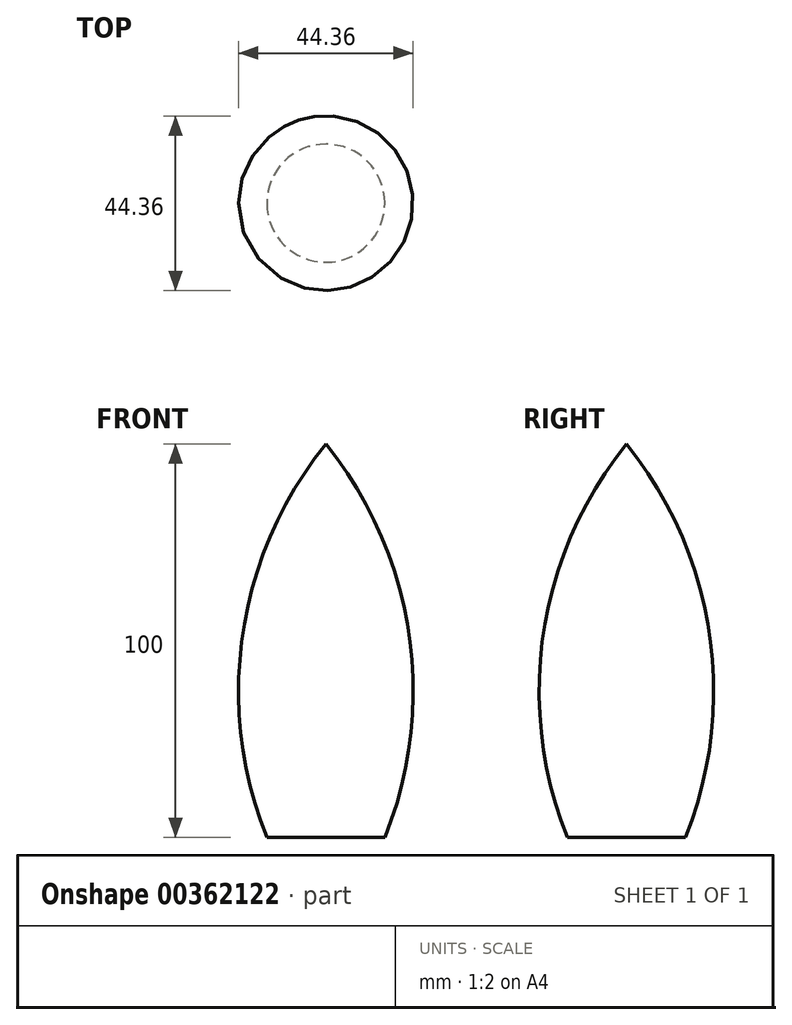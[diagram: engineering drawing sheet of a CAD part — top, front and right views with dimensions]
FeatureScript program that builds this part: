
annotation { "Feature Type Name" : "Feature", "Feature Type Description" : "" }
export const myFeature = defineFeature(function(context is Context, id is Id, definition is map)
    precondition{}
    {
        {
            var Q0;
            Q0=qCreatedBy(makeId("Front.planeOp"),FACE);
            var sketch = newSketch(context, id + "F0", { "sketchPlane" : qUnion([Q0])});
            skArc(sketch, "E0", {"start": v(0, 100) * mm, "mid": v(-21.07, 52.04) * mm, "end": v(-15, 0) * mm});
            skLineSegment(sketch, "E1", {"start": v(0, 100) * mm, "end": v(0, 0) * mm});
            skLineSegment(sketch, "E2", {"start": v(0, 0) * mm, "end": v(-15, 0) * mm});
            skSolve(sketch);
        }
        {
            var Q0;
            Q0=makeQuery(id+"F0.imprint","IMPRINT",FACE,{"disambiguationData":[TD([[makeQuery(id+"F0.imprint","IMPRINT",EDGE,{"derivedFrom":sQuery(id+"F0.wireOp",EDGE,"E0")}),1.0]])]});
            var Q1;
            Q1=sQuery(id+"F0.wireOp",EDGE,"E1");
            revolve(context, id + "F1", {"surfaceOperationType" : NewSurfaceOperationType.NEW, "entities" : qUnion([Q0]), "axis" : qUnion([Q1]), "revolveType" : RevolveType.FULL});
        }
    });
